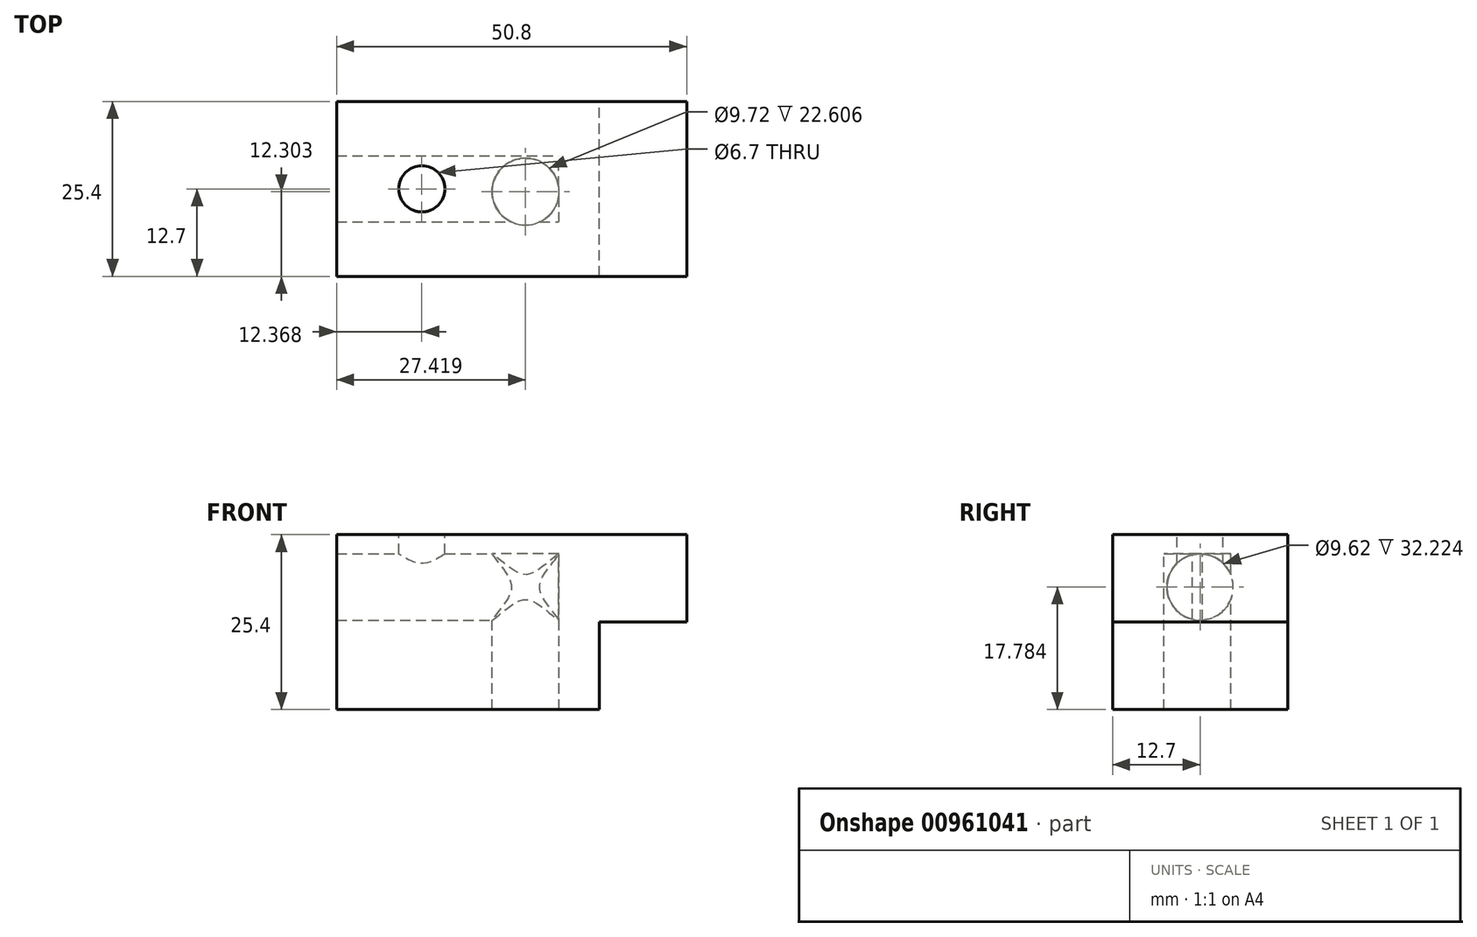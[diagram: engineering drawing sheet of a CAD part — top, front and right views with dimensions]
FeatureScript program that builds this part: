
annotation { "Feature Type Name" : "Feature", "Feature Type Description" : "" }
export const myFeature = defineFeature(function(context is Context, id is Id, definition is map)
    precondition{}
    {
        {
            var Q0;
            Q0=qCreatedBy(makeId("Front.planeOp"),FACE);
            var sketch = newSketch(context, id + "F0", { "sketchPlane" : qUnion([Q0])});
            skLineSegment(sketch, "E0", {"start": v(-22.56, -10.63) * mm, "end": v(-22.56, 14.77) * mm});
            skLineSegment(sketch, "E1", {"start": v(-22.56, 14.77) * mm, "end": v(28.24, 14.77) * mm});
            skLineSegment(sketch, "E2", {"start": v(28.24, 14.77) * mm, "end": v(28.24, 2.07) * mm});
            skLineSegment(sketch, "E3", {"start": v(28.24, 2.07) * mm, "end": v(15.54, 2.07) * mm});
            skLineSegment(sketch, "E4", {"start": v(15.54, 2.07) * mm, "end": v(15.54, -10.63) * mm});
            skLineSegment(sketch, "E5", {"start": v(15.54, -10.63) * mm, "end": v(-22.56, -10.63) * mm});
            skSolve(sketch);
        }
        {
            var Q0;
            Q0=makeQuery(id+"F0.imprint","IMPRINT",FACE,{"disambiguationData":[TD([[makeQuery(id+"F0.imprint","IMPRINT",EDGE,{"derivedFrom":sQuery(id+"F0.wireOp",EDGE,"E0")}),-1.0]])]});
            extrude(context, id + "F1", {"entities" : qUnion([Q0]), "depth" : 25.4 * mm, "offsetDistance" : 25.4 * mm});
        }
        {
            var Q0;
            Q0=qCreatedBy(makeId("Right.planeOp"),FACE);
            cPlane(context, id + "F2", {"entities" : qUnion([Q0]), "cplaneType" : CPlaneType.OFFSET, "offset" : 9.66 * mm, "width" : 152.4 * mm, "height" : 152.4 * mm});
        }
        {
            var Q0;
            Q0=qCreatedBy(id+"F2.planeOp",FACE);
            var sketch = newSketch(context, id + "F3", { "sketchPlane" : qUnion([Q0])});
            skCircle(sketch, "E6", {"center": v(-12.7, 7.15) * mm, "radius": 4.81 * mm});
            skSolve(sketch);
        }
        {
            var Q0;
            Q0 = qSketchRegion(id + "F3", true);
            extrude(context, id + "F4", {"entities" : qUnion([Q0]), "operationType" : NewBodyOperationType.REMOVE, "oppositeDirection" : true, "depth" : 50.8 * mm, "offsetDistance" : 25.4 * mm});
        }
        {
            var Q0;
            Q0=makeQuery(id+"F1.opExtrude","SWEPT_FACE",FACE,{"disambiguationData":[OSD([sQuery(id+"F0.wireOp",EDGE,"E1")])]});
            cPlane(context, id + "F5", {"entities" : qUnion([Q0]), "cplaneType" : CPlaneType.OFFSET, "offset" : 2.8 * mm, "oppositeDirection" : true, "width" : 152.4 * mm, "height" : 152.4 * mm});
        }
        {
            var Q0;
            Q0=qCreatedBy(id+"F5.planeOp",FACE);
            var sketch = newSketch(context, id + "F6", { "sketchPlane" : qUnion([Q0])});
            skCircle(sketch, "E7", {"center": v(4.86, -13.1) * mm, "radius": 4.86 * mm});
            skPoint(sketch, "E7.first.point", {"position": v(0, -13.01) * mm});
            skPoint(sketch, "E7.second.point", {"position": v(9.72, -12.98) * mm});
            skPoint(sketch, "E7.third.point", {"position": v(4.89, -8.24) * mm});
            skSolve(sketch);
        }
        {
            var Q0;
            Q0 = qSketchRegion(id + "F6", true);
            extrude(context, id + "F7", {"entities" : qUnion([Q0]), "operationType" : NewBodyOperationType.REMOVE, "oppositeDirection" : true, "depth" : 25.4 * mm, "offsetDistance" : 25.4 * mm});
        }
        {
            var Q0;
            Q0=makeQuery(id+"F1.opExtrude","SWEPT_FACE",FACE,{"disambiguationData":[OSD([sQuery(id+"F0.wireOp",EDGE,"E1")])]});
            var sketch = newSketch(context, id + "F8", { "sketchPlane" : qUnion([Q0])});
            skCircle(sketch, "E8", {"center": v(-10.2, -12.7) * mm, "radius": 3.35 * mm});
            skPoint(sketch, "E8.centerSnap0", {"position": v(-22.56, -12.7) * mm});
            skSolve(sketch);
        }
        {
            var Q0;
            Q0 = qSketchRegion(id + "F8", true);
            extrude(context, id + "F9", {"entities" : qUnion([Q0]), "operationType" : NewBodyOperationType.REMOVE, "oppositeDirection" : true, "depth" : 7.62 * mm, "offsetDistance" : 25.4 * mm});
        }
    });
